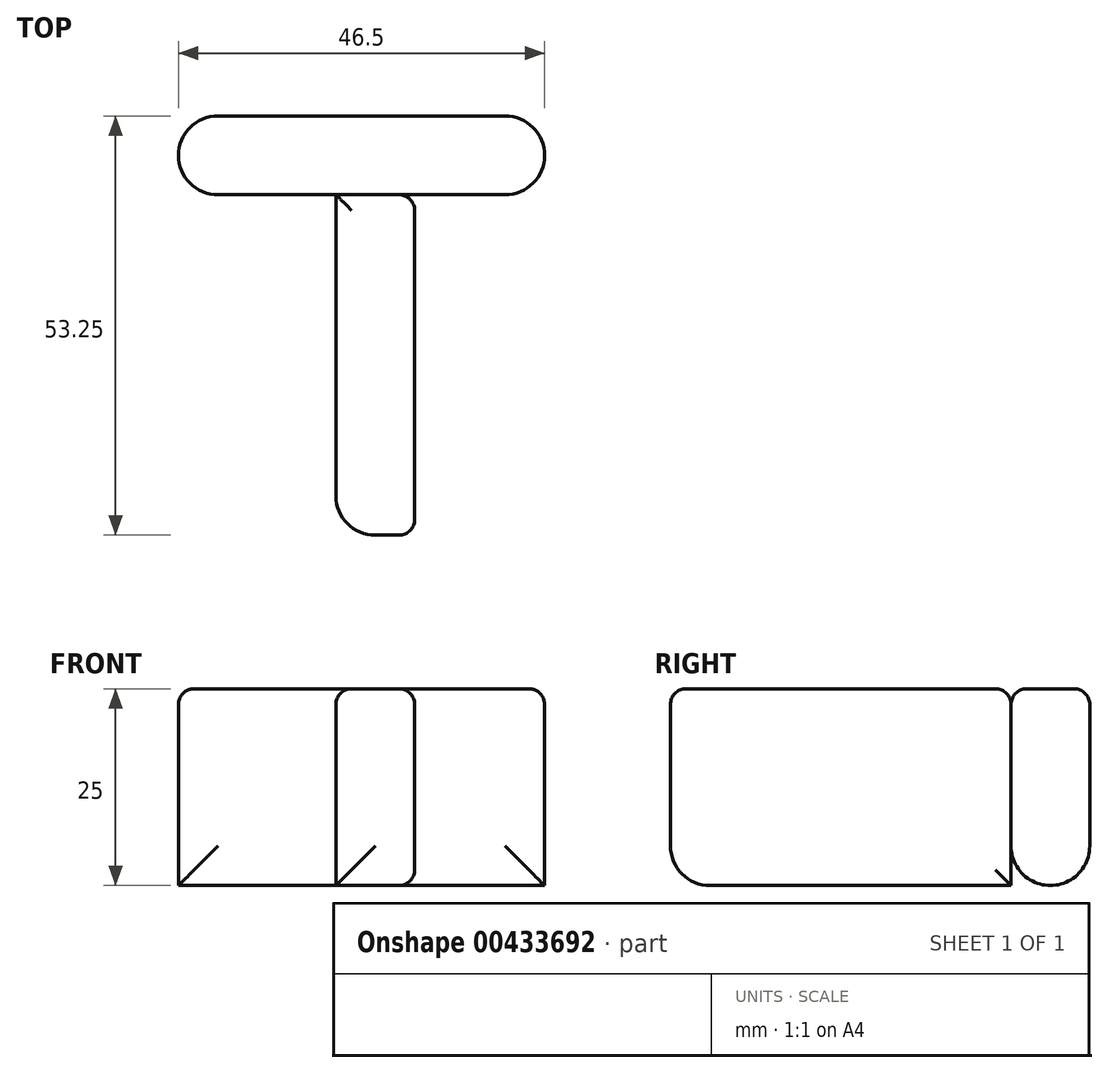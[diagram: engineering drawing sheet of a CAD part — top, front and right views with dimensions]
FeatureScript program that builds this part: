
annotation { "Feature Type Name" : "Feature", "Feature Type Description" : "" }
export const myFeature = defineFeature(function(context is Context, id is Id, definition is map)
    precondition{}
    {
        {
            var Q0;
            Q0=qCreatedBy(makeId("Top.planeOp"),FACE);
            var sketch = newSketch(context, id + "F0", { "sketchPlane" : qUnion([Q0])});
            skLineSegment(sketch, "E0", {"start": v(0, 0) * mm, "end": v(0, -40) * mm});
            skLineSegment(sketch, "E1", {"start": v(0, 0) * mm, "end": v(-20, 0) * mm});
            skLineSegment(sketch, "E2", {"start": v(0, 0) * mm, "end": v(6.5, 0) * mm});
            skLineSegment(sketch, "E3", {"start": v(6.5, 0) * mm, "end": v(26.5, 0) * mm});
            skLineSegment(sketch, "E4", {"start": v(9.75, 0) * mm, "end": v(9.75, -40) * mm});
            skLineSegment(sketch, "E5", {"start": v(-20, 0) * mm, "end": v(-20, 10) * mm});
            skLineSegment(sketch, "E6", {"start": v(-20, 10) * mm, "end": v(26.5, 10) * mm});
            skLineSegment(sketch, "E7", {"start": v(26.5, 10) * mm, "end": v(26.5, 0) * mm});
            skLineSegment(sketch, "E8", {"start": v(2.25, -40) * mm, "end": v(9.75, -40) * mm});
            skPoint(sketch, "E9.startSnap0", {"position": v(6, -40) * mm});
            skSolve(sketch);
        }
        {
            var Q0;
            Q0=qCreatedBy(makeId("Top.planeOp"),FACE);
            var sketch = newSketch(context, id + "F1", { "sketchPlane" : qUnion([Q0])});
            skLineSegment(sketch, "E10", {"start": v(0, 0) * mm, "end": v(0, -43.25) * mm});
            skLineSegment(sketch, "E11", {"start": v(0, -43.25) * mm, "end": v(10, -43.25) * mm});
            skLineSegment(sketch, "E12", {"start": v(10, -43.25) * mm, "end": v(10, 0) * mm});
            skLineSegment(sketch, "E13", {"start": v(-1.96, 0) * mm, "end": v(10, 0) * mm});
            skSolve(sketch);
        }
        {
            var Q0;
            Q0 = qSketchRegion(id + "F1", true);
            var Q1;
            Q1=makeQuery(id+"F0.imprint","IMPRINT",FACE,{"disambiguationData":[TD([[makeQuery(id+"F0.imprint","IMPRINT",EDGE,{"derivedFrom":sQuery(id+"F0.wireOp",EDGE,"E1")}),-1.0]])]});
            extrude(context, id + "F2", {"entities" : qUnion([Q0, Q1]), "depth" : 25 * mm});
        }
        {
            var Q0;
            Q0=makeQuery(id+"F2.opExtrude","CAP_FACE",FACE,{"disambiguationData":[OSD([sQuery(id+"F0.wireOp",EDGE,"E1"),sQuery(id+"F0.wireOp",EDGE,"E2"),sQuery(id+"F0.wireOp",EDGE,"E3"),sQuery(id+"F0.wireOp",EDGE,"E5"),sQuery(id+"F0.wireOp",EDGE,"E6"),sQuery(id+"F0.wireOp",EDGE,"E7")])],"isStart":false});
            var Q1;
            Q1=makeQuery(id+"F2.opExtrude","CAP_FACE",FACE,{"disambiguationData":[OSD([sQuery(id+"F1.wireOp",EDGE,"E10"),sQuery(id+"F1.wireOp",EDGE,"E11"),sQuery(id+"F1.wireOp",EDGE,"E12"),sQuery(id+"F1.wireOp",EDGE,"E13")])],"isStart":false});
            var Q2;
            Q2=makeQuery(id+"F2.opExtrude","SWEPT_FACE",FACE,{"disambiguationData":[OSD([sQuery(id+"F1.wireOp",EDGE,"E12")])]});
            fillet(context, id + "F3", {"entities" : qUnion([Q0, Q1, Q2]), "radius" : 2 * mm, "tangentPropagation" : true, "allowEdgeOverflow" : false});
        }
        {
            var Q0;
            Q0=makeQuery(id+"F2.opExtrude","SWEPT_FACE",FACE,{"disambiguationData":[OSD([sQuery(id+"F1.wireOp",EDGE,"E11")])]});
            fillet(context, id + "F4", {"entities" : qUnion([Q0]), "radius" : 5 * mm, "tangentPropagation" : true, "allowEdgeOverflow" : false});
        }
        {
            var Q0;
            Q0=makeQuery(id+"F2.opExtrude","SWEPT_FACE",FACE,{"disambiguationData":[OSD([sQuery(id+"F0.wireOp",EDGE,"E1"),sQuery(id+"F0.wireOp",EDGE,"E2"),sQuery(id+"F0.wireOp",EDGE,"E3")])]});
            fillet(context, id + "F5", {"entities" : qUnion([Q0]), "radius" : 5 * mm, "tangentPropagation" : true, "allowEdgeOverflow" : false});
        }
        {
            var Q0;
            Q0=makeQuery(id+"F2.opExtrude","SWEPT_FACE",FACE,{"disambiguationData":[OSD([sQuery(id+"F0.wireOp",EDGE,"E6")])]});
            fillet(context, id + "F6", {"entities" : qUnion([Q0]), "radius" : 5 * mm, "tangentPropagation" : true, "allowEdgeOverflow" : false});
        }
    });
